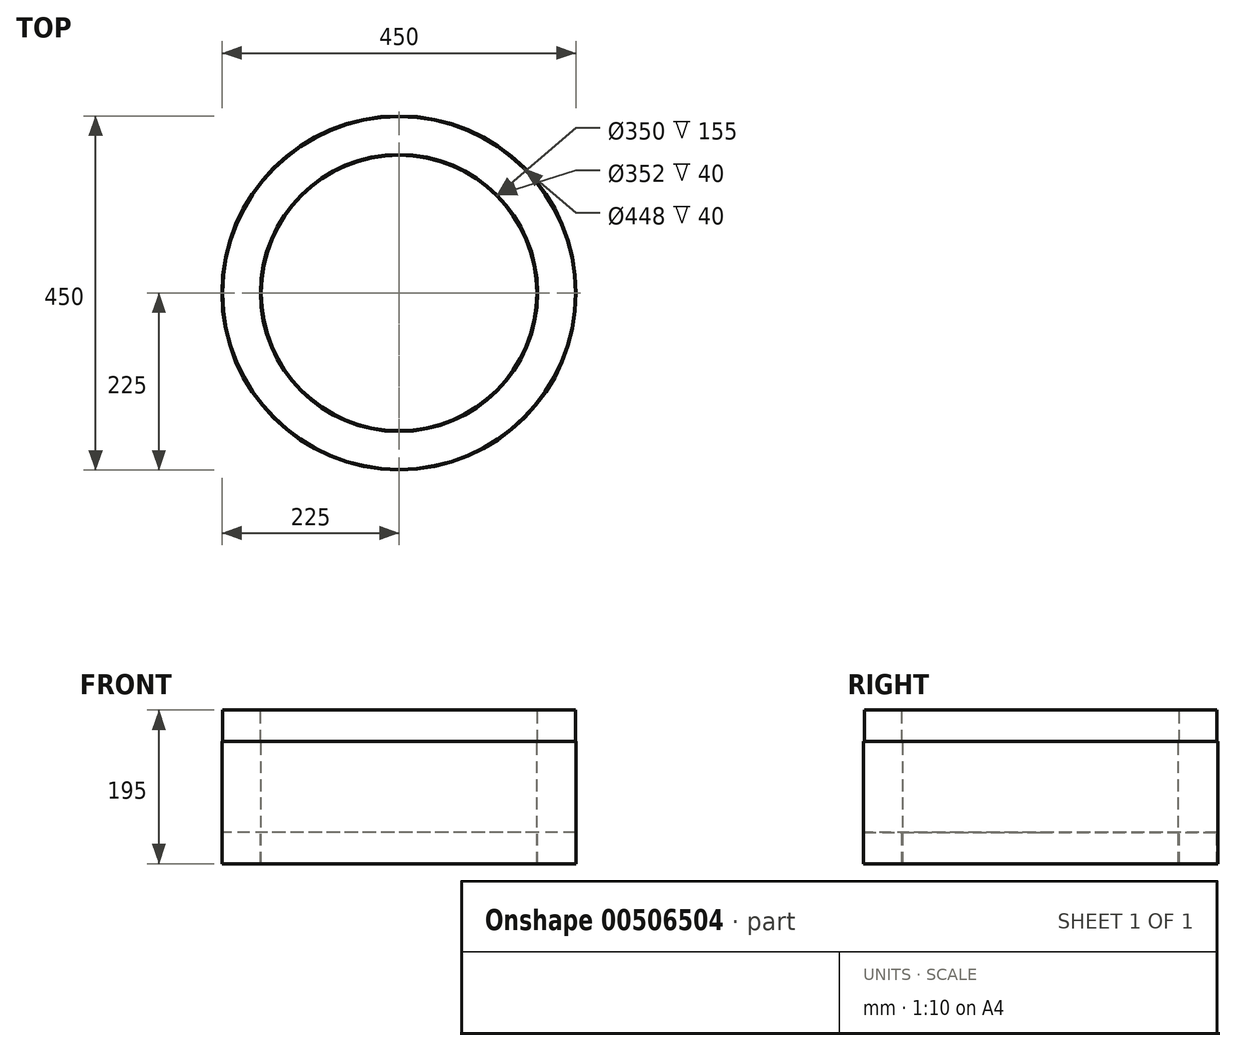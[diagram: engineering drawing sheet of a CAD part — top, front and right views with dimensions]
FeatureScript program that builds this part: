
annotation { "Feature Type Name" : "Feature", "Feature Type Description" : "" }
export const myFeature = defineFeature(function(context is Context, id is Id, definition is map)
    precondition{}
    {
        {
            var Q0;
            Q0=qCreatedBy(makeId("Front.planeOp"),FACE);
            var sketch = newSketch(context, id + "F0", { "sketchPlane" : qUnion([Q0])});
            skLineSegment(sketch, "E0", {"start": v(0, 74.87) * mm, "end": v(0, -73.71) * mm, "construction": true});
            skLineSegment(sketch, "E1", {"start": v(0, 374.84) * mm, "end": v(0, -528.94) * mm, "construction": true});
            skLineSegment(sketch, "E2", {"start": v(-175, -489.75) * mm, "end": v(-175, -334.75) * mm});
            skLineSegment(sketch, "E3", {"start": v(-175, -334.75) * mm, "end": v(-176, -334.75) * mm});
            skLineSegment(sketch, "E4", {"start": v(-176, -334.75) * mm, "end": v(-176, -294.75) * mm});
            skLineSegment(sketch, "E5", {"start": v(-176, -294.75) * mm, "end": v(-224, -294.75) * mm});
            skLineSegment(sketch, "E6", {"start": v(-224, -294.75) * mm, "end": v(-224, -334.75) * mm});
            skLineSegment(sketch, "E7", {"start": v(-224, -334.75) * mm, "end": v(-225, -334.75) * mm});
            skLineSegment(sketch, "E8", {"start": v(-225, -334.75) * mm, "end": v(-225, -489.75) * mm});
            skLineSegment(sketch, "E9", {"start": v(-225, -489.75) * mm, "end": v(-224, -489.75) * mm});
            skLineSegment(sketch, "E10", {"start": v(-224, -489.75) * mm, "end": v(-224, -449.75) * mm});
            skLineSegment(sketch, "E11", {"start": v(-224, -449.75) * mm, "end": v(-176, -449.75) * mm});
            skLineSegment(sketch, "E12", {"start": v(-176, -449.75) * mm, "end": v(-176, -489.75) * mm});
            skLineSegment(sketch, "E13", {"start": v(-176, -489.75) * mm, "end": v(-175, -489.75) * mm});
            skSolve(sketch);
        }
        {
            var Q0;
            Q0=qSketchRegion(id+"F0",true);
            var Q1;
            Q1=sQuery(id+"F0.wireOp",EDGE,"E1");
            revolve(context, id + "F1", {"entities" : qUnion([Q0]), "axis" : qUnion([Q1]), "revolveType" : RevolveType.FULL});
        }
    });
